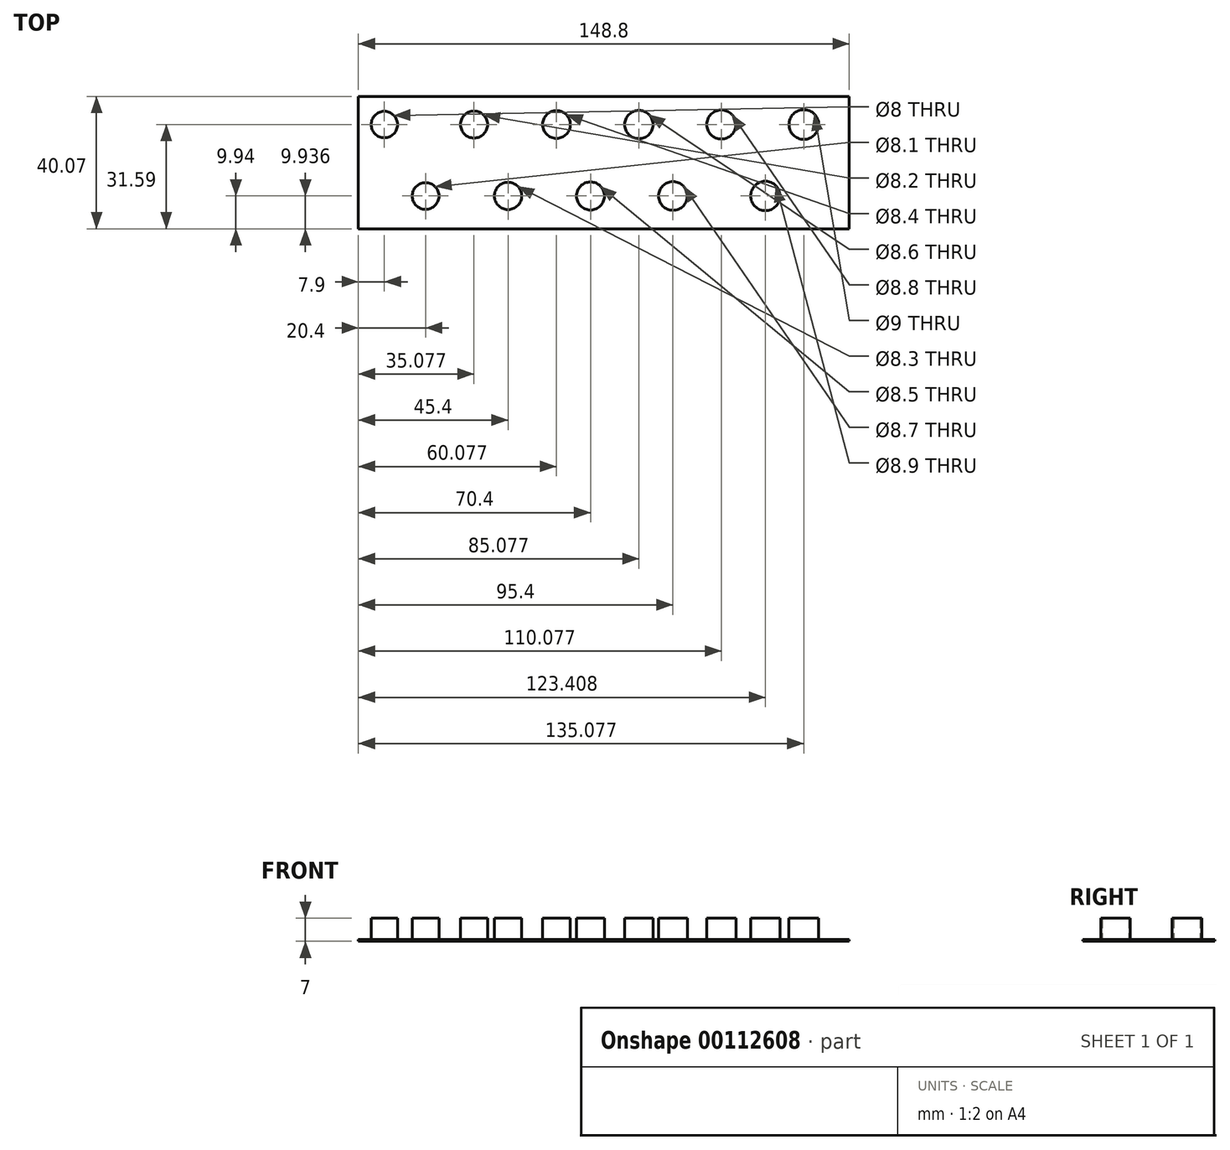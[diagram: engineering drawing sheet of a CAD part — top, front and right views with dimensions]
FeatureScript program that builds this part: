
annotation { "Feature Type Name" : "Feature", "Feature Type Description" : "" }
export const myFeature = defineFeature(function(context is Context, id is Id, definition is map)
    precondition{}
    {
        {
            var Q0;
            Q0=qCreatedBy(makeId("Top.planeOp"),FACE);
            var sketch = newSketch(context, id + "F0", { "sketchPlane" : qUnion([Q0])});
            skLineSegment(sketch, "E0.bottom", {"start": v(-77.3, -40.07) * mm, "end": v(71.51, -40.07) * mm});
            skLineSegment(sketch, "E0.top", {"start": v(-77.3, 0) * mm, "end": v(71.51, 0) * mm});
            skLineSegment(sketch, "E0.left", {"start": v(-77.3, -40.07) * mm, "end": v(-77.3, 0) * mm});
            skLineSegment(sketch, "E0.right", {"start": v(71.51, -40.07) * mm, "end": v(71.51, 0) * mm});
            skCircle(sketch, "E1", {"center": v(-69.4, -8.48) * mm, "radius": 4 * mm});
            skCircle(sketch, "E2", {"center": v(-56.9, -30.13) * mm, "radius": 4.05 * mm});
            skLineSegment(sketch, "E3", {"start": v(-69.4, -8.48) * mm, "end": v(76.8, -8.48) * mm, "construction": true});
            skLineSegment(sketch, "E4", {"start": v(-69.4, -8.48) * mm, "end": v(-56.9, -30.13) * mm, "construction": true});
            skCircle(sketch, "E5", {"center": v(-42.21, -8.48) * mm, "radius": 4.1 * mm});
            skCircle(sketch, "E6.1.0.0", {"center": v(-17.21, -8.48) * mm, "radius": 4.2 * mm});
            skCircle(sketch, "E6.2.0.0", {"center": v(7.79, -8.48) * mm, "radius": 4.3 * mm});
            skCircle(sketch, "E6.3.0.0", {"center": v(32.79, -8.48) * mm, "radius": 4.4 * mm});
            skCircle(sketch, "E6.4.0.0", {"center": v(57.79, -8.48) * mm, "radius": 4.5 * mm});
            skLineSegment(sketch, "E7", {"start": v(-56.9, -30.13) * mm, "end": v(67.67, -30.13) * mm, "construction": true});
            skCircle(sketch, "E8.1.0.0", {"center": v(-31.9, -30.13) * mm, "radius": 4.15 * mm});
            skCircle(sketch, "E8.2.0.0", {"center": v(-6.9, -30.13) * mm, "radius": 4.25 * mm});
            skCircle(sketch, "E8.3.0.0", {"center": v(18.1, -30.13) * mm, "radius": 4.35 * mm});
            skLineSegment(sketch, "E8.direction1", {"start": v(-56.9, -30.13) * mm, "end": v(-31.9, -30.13) * mm, "construction": true});
            skCircle(sketch, "E9", {"center": v(46.12, -30.13) * mm, "radius": 4.45 * mm});
            skSolve(sketch);
        }
        {
            var Q0;
            Q0=makeQuery(id+"F0.imprint","IMPRINT",FACE,{"disambiguationData":[TD([[makeQuery(id+"F0.imprint","IMPRINT",EDGE,{"derivedFrom":sQuery(id+"F0.wireOp",EDGE,"E2")}),1.0]])]});
            var Q1;
            Q1=makeQuery(id+"F0.imprint","IMPRINT",FACE,{"disambiguationData":[TD([[makeQuery(id+"F0.imprint","IMPRINT",EDGE,{"derivedFrom":sQuery(id+"F0.wireOp",EDGE,"E8.1.0.0")}),1.0]])]});
            var Q2;
            Q2=makeQuery(id+"F0.imprint","IMPRINT",FACE,{"disambiguationData":[TD([[makeQuery(id+"F0.imprint","IMPRINT",EDGE,{"derivedFrom":sQuery(id+"F0.wireOp",EDGE,"E1")}),1.0]])]});
            var Q3;
            Q3=makeQuery(id+"F0.imprint","IMPRINT",FACE,{"disambiguationData":[TD([[makeQuery(id+"F0.imprint","IMPRINT",EDGE,{"derivedFrom":sQuery(id+"F0.wireOp",EDGE,"E5")}),1.0]])]});
            var Q4;
            Q4=makeQuery(id+"F0.imprint","IMPRINT",FACE,{"disambiguationData":[TD([[makeQuery(id+"F0.imprint","IMPRINT",EDGE,{"derivedFrom":sQuery(id+"F0.wireOp",EDGE,"E6.1.0.0")}),1.0]])]});
            var Q5;
            Q5=makeQuery(id+"F0.imprint","IMPRINT",FACE,{"disambiguationData":[TD([[makeQuery(id+"F0.imprint","IMPRINT",EDGE,{"derivedFrom":sQuery(id+"F0.wireOp",EDGE,"E8.2.0.0")}),1.0]])]});
            var Q6;
            Q6=makeQuery(id+"F0.imprint","IMPRINT",FACE,{"disambiguationData":[TD([[makeQuery(id+"F0.imprint","IMPRINT",EDGE,{"derivedFrom":sQuery(id+"F0.wireOp",EDGE,"E8.3.0.0")}),1.0]])]});
            var Q7;
            Q7=makeQuery(id+"F0.imprint","IMPRINT",FACE,{"disambiguationData":[TD([[makeQuery(id+"F0.imprint","IMPRINT",EDGE,{"derivedFrom":sQuery(id+"F0.wireOp",EDGE,"E6.2.0.0")}),1.0]])]});
            var Q8;
            Q8=makeQuery(id+"F0.imprint","IMPRINT",FACE,{"disambiguationData":[TD([[makeQuery(id+"F0.imprint","IMPRINT",EDGE,{"derivedFrom":sQuery(id+"F0.wireOp",EDGE,"E6.3.0.0")}),1.0]])]});
            var Q9;
            Q9=makeQuery(id+"F0.imprint","IMPRINT",FACE,{"disambiguationData":[TD([[makeQuery(id+"F0.imprint","IMPRINT",EDGE,{"derivedFrom":sQuery(id+"F0.wireOp",EDGE,"E9")}),1.0]])]});
            var Q10;
            Q10=makeQuery(id+"F0.imprint","IMPRINT",FACE,{"disambiguationData":[TD([[makeQuery(id+"F0.imprint","IMPRINT",EDGE,{"derivedFrom":sQuery(id+"F0.wireOp",EDGE,"E6.4.0.0")}),1.0]])]});
            var Q11;
            Q11=sQuery(id+"F0.wireOp",EDGE,"E8.1.0.0");
            var Q12;
            Q12=sQuery(id+"F0.wireOp",EDGE,"E8.2.0.0");
            var Q13;
            Q13=sQuery(id+"F0.wireOp",EDGE,"E6.1.0.0");
            var Q14;
            Q14=sQuery(id+"F0.wireOp",EDGE,"E1");
            var Q15;
            Q15=sQuery(id+"F0.wireOp",EDGE,"E2");
            var Q16;
            Q16=sQuery(id+"F0.wireOp",EDGE,"E9");
            var Q17;
            Q17=sQuery(id+"F0.wireOp",EDGE,"E8.3.0.0");
            var Q18;
            Q18=sQuery(id+"F0.wireOp",EDGE,"E5");
            var Q19;
            Q19=sQuery(id+"F0.wireOp",EDGE,"E6.2.0.0");
            var Q20;
            Q20=sQuery(id+"F0.wireOp",EDGE,"E6.3.0.0");
            var Q21;
            Q21=sQuery(id+"F0.wireOp",EDGE,"E6.4.0.0");
            extrude(context, id + "F1", {"entities" : qUnion([Q0, Q1, Q2, Q3, Q4, Q5, Q6, Q7, Q8, Q9, Q10]), "surfaceEntities" : qUnion([Q11, Q12, Q13, Q14, Q15, Q16, Q17, Q18, Q19, Q20, Q21]), "depth" : 7 * mm});
        }
        {
            var Q0;
            {var subQ0=sQuery(id+"F0.wireOp",EDGE,"E0.bottom");Q0=makeQuery(id+"F0.imprint","IMPRINT",FACE,{"disambiguationData":[TD([[makeQuery(id+"F0.imprint","IMPRINT",EDGE,{"derivedFrom":subQ0}),1.0]])]});}
            extrude(context, id + "F2", {"entities" : qUnion([Q0]), "depth" : 0.5 * mm});
        }
    });
